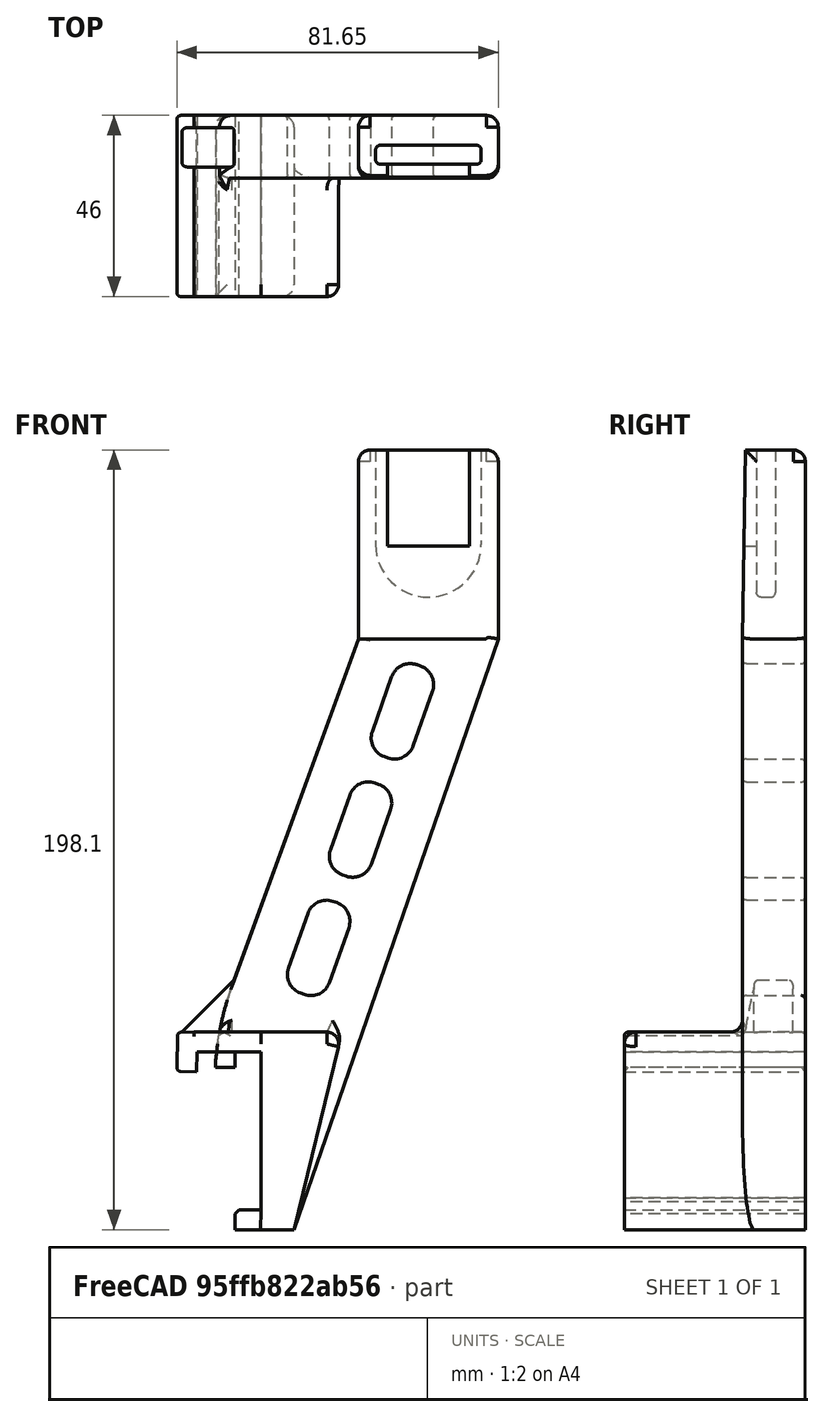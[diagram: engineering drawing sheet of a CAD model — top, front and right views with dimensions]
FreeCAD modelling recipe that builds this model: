
FCSTD DOCUMENT  (FreeCAD 0.18R16146 (Git))
Label: FillerPrusaSource
License: All rights reserved
LicenseURL: http://en.wikipedia.org/wiki/All_rights_reserved
objects: Part::Box×5, Part::Cut×3, Part::Fillet×3, Part::Fuse×3, Part::Feature×2
note: 16 computed .brp shape members not serialized (recipe doc carries the construction recipe); baked Part::Feature solids carry a one-line shape summary decoded from their .brp

FEATURE [Part::Feature] Part__Feature  label="Filler Prusa MK2 v7"
  shape: bbox 72.68 x 46.01 x 199.1 mm, 130 faces (baked)
FEATURE [Part::Feature] Part__Feature001  label="Filler Prusa MK2 v008"
  shape: bbox 72.68 x 46.01 x 199.1 mm, 129 faces (baked)
FEATURE [Part::Box] Box  label="Cubeadd"
  AttacherType = Attacher::AttachEngine3D
  Height = 5
  Length = 17
  Placement = pos=(-10.35,0,45.2) rot=(0,0,1;0rad)
  Width = 46
FEATURE [Part::Box] Box001  label="Cubeadd001"
  AttacherType = Attacher::AttachEngine3D
  Height = 5
  Length = 16
  Placement = pos=(-9.35,0,40.2) rot=(0,0,1;0rad)
  Width = 46
FEATURE [Part::Cut] Cut
  Base = -> Part__Feature001
  Tool = -> Box001
FEATURE [Part::Box] Box002  label="Cubeadd002"
  AttacherType = Attacher::AttachEngine3D
  Height = 5
  Length = 10
  Placement = pos=(-14.6,0,50.2) rot=(0,1,0;1.58825rad)
  Width = 46
FEATURE [Part::Box] Box003  label="Cubeadd003"
  AttacherType = Attacher::AttachEngine3D
  Height = 15
  Length = 10
  Placement = pos=(-8.32883,0,8.38418) rot=(0,1,0;1.58825rad)
  Width = 46
FEATURE [Part::Cut] Cut002
  Base = -> Cut
  Tool = -> Box003
FEATURE [Part::Cut] Cut001
  Base = -> Part__Feature001
  Tool = -> Box001
FEATURE [Part::Fillet] Fillet
  Base = -> Box002
  Edges = 6 edges r=1: [Edge1,Edge3,Edge4,Edge8,Edge9,Edge11]
FEATURE [Part::Fillet] Fillet001
  Base = -> Box
  Edges = 2 edges r=1: [Edge10,Edge12]
FEATURE [Part::Box] Box004  label="Cube"
  AttacherType = Attacher::AttachEngine3D
  Height = 20
  Length = 6.8
  Placement = pos=(-13.5033,32.9,50.1062) rot=(0,1,0;0.785398rad)
  Width = 10
FEATURE [Part::Fillet] Fillet002
  Base = -> Box004
  Edges = 2 edges r=1: [Edge1,Edge3]
FEATURE [Part::Fuse] Fusion
  Base = -> Cut002
  Tool = -> Fillet001
FEATURE [Part::Fuse] Fusion001
  Base = -> Fillet002
  Tool = -> Fusion
FEATURE [Part::Fuse] Fusion002
  Base = -> Fillet
  Tool = -> Fusion001
